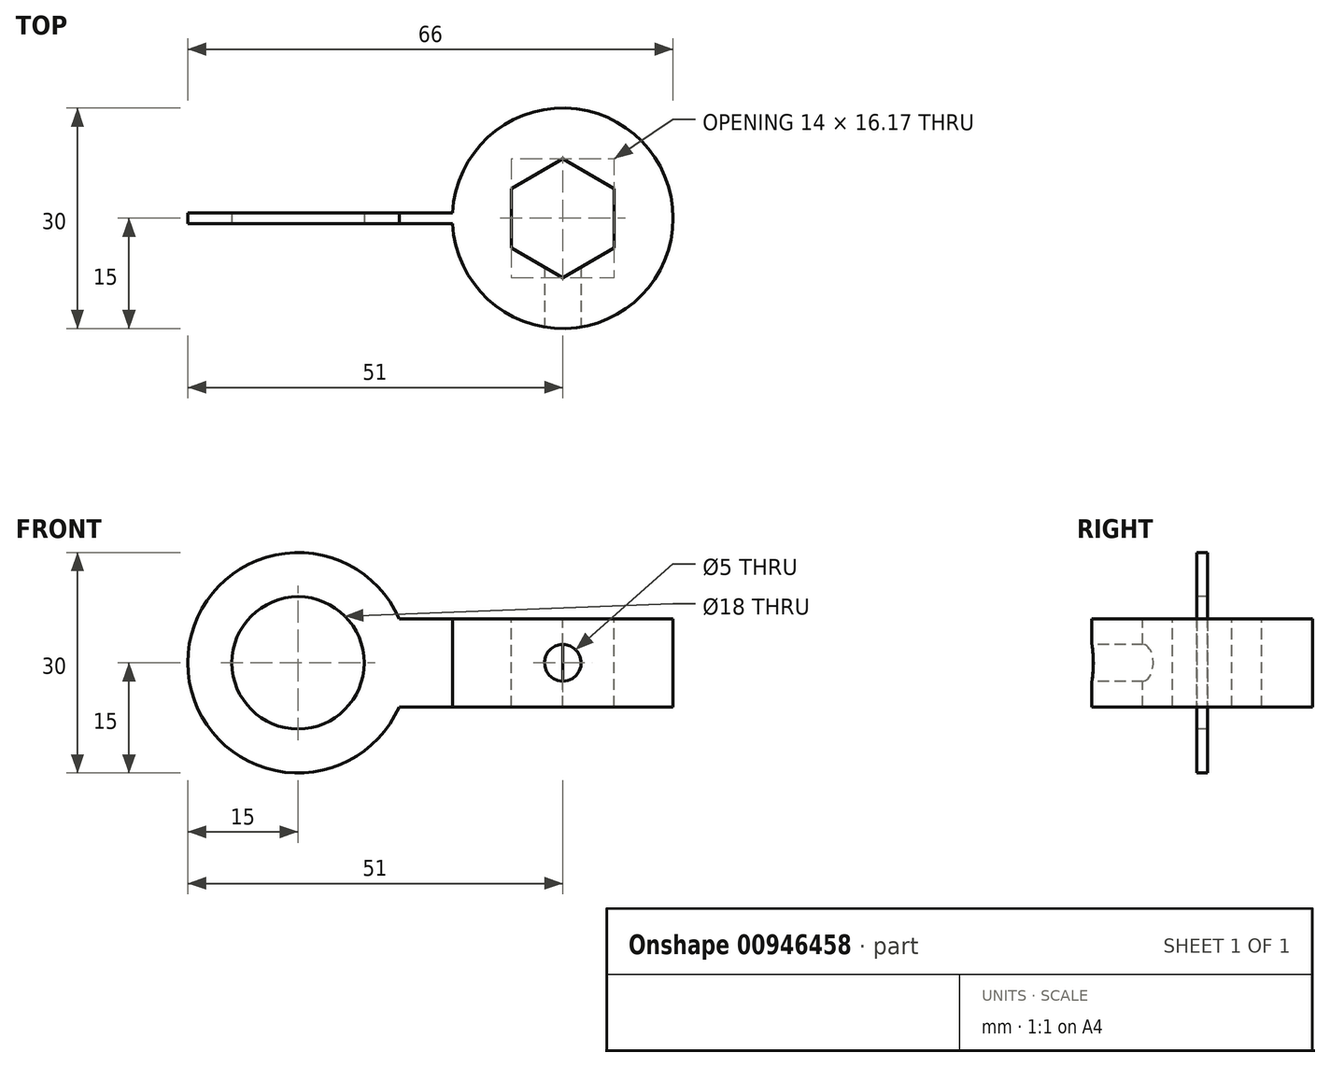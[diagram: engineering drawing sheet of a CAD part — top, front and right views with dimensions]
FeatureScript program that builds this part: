
annotation { "Feature Type Name" : "Feature", "Feature Type Description" : "" }
export const myFeature = defineFeature(function(context is Context, id is Id, definition is map)
    precondition{}
    {
        {
            var Q0;
            Q0=qCreatedBy(makeId("Top.planeOp"),FACE);
            var sketch = newSketch(context, id + "F0", { "sketchPlane" : qUnion([Q0])});
            skCircle(sketch, "E0", {"center": v(0, 0) * mm, "radius": 15 * mm});
            skSolve(sketch);
        }
        {
            var Q0;
            Q0 = qSketchRegion(id + "F0", true);
            extrude(context, id + "F1", {"entities" : qUnion([Q0]), "depth" : 12 * mm, "offsetDistance" : 25 * mm});
        }
        {
            var Q0;
            Q0=makeQuery(id+"F1.opExtrude","CAP_FACE",FACE,{"disambiguationData":[OSD([sQuery(id+"F0.wireOp",EDGE,"E0")])],"isStart":false});
            var sketch = newSketch(context, id + "F2", { "sketchPlane" : qUnion([Q0])});
            skCircle(sketch, "E1.cCircle", {"center": v(0, 0) * mm, "radius": 7 * mm, "construction": true});
            skLineSegment(sketch, "E1.0", {"start": v(7, 4.04) * mm, "end": v(7, -4.04) * mm});
            skLineSegment(sketch, "E1.1", {"start": v(7, -4.04) * mm, "end": v(0, -8.08) * mm});
            skLineSegment(sketch, "E1.2", {"start": v(0, -8.08) * mm, "end": v(-7, -4.04) * mm});
            skLineSegment(sketch, "E1.3", {"start": v(-7, -4.04) * mm, "end": v(-7, 4.04) * mm});
            skLineSegment(sketch, "E1.4", {"start": v(-7, 4.04) * mm, "end": v(0, 8.08) * mm});
            skLineSegment(sketch, "E1.5", {"start": v(0, 8.08) * mm, "end": v(7, 4.04) * mm});
            skPoint(sketch, "E1.0.midPoint", {"position": v(7, 0) * mm});
            skSolve(sketch);
        }
        {
            var Q0;
            Q0 = qSketchRegion(id + "F2", true);
            extrude(context, id + "F3", {"entities" : qUnion([Q0]), "operationType" : NewBodyOperationType.REMOVE, "endBound" : BoundingType.THROUGH_ALL, "oppositeDirection" : true, "depth" : 25 * mm, "offsetDistance" : 25 * mm});
        }
        {
            var Q0;
            Q0=qCreatedBy(makeId("Front.planeOp"),FACE);
            var sketch = newSketch(context, id + "F4", { "sketchPlane" : qUnion([Q0])});
            skLineSegment(sketch, "E2", {"start": v(0, 0) * mm, "end": v(-15, 0) * mm, "construction": true});
            skLineSegment(sketch, "E3", {"start": v(0, 0) * mm, "end": v(0, 12) * mm, "construction": true});
            skLineSegment(sketch, "E4", {"start": v(0, 12) * mm, "end": v(-15, 12) * mm, "construction": true});
            skLineSegment(sketch, "E5.bottom", {"start": v(-15, 0) * mm, "end": v(-21, 0) * mm});
            skLineSegment(sketch, "E5.top", {"start": v(-15, 12) * mm, "end": v(-21, 12) * mm});
            skLineSegment(sketch, "E5.left", {"start": v(-15, 0) * mm, "end": v(-15, 12) * mm});
            skLineSegment(sketch, "E5.right", {"start": v(-21, 0) * mm, "end": v(-21, 12) * mm});
            skPoint(sketch, "E6", {"position": v(-21, 6) * mm});
            skCircle(sketch, "E7", {"center": v(-36, 6) * mm, "radius": 15 * mm});
            skSolve(sketch);
        }
        {
            var Q0;
            Q0 = qSketchRegion(id + "F4", true);
            extrude(context, id + "F5", {"entities" : qUnion([Q0]), "endBound" : BoundingType.SYMMETRIC, "depth" : 1.5 * mm, "offsetDistance" : 25 * mm});
        }
        {
            var Q0;
            Q0=makeQuery(id+"F5.opExtrude","CAP_FACE",FACE,{"disambiguationData":[OSD([sQuery(id+"F4.wireOp",EDGE,"E7")])],"isStart":false});
            var sketch = newSketch(context, id + "F6", { "sketchPlane" : qUnion([Q0])});
            skCircle(sketch, "E8", {"center": v(-36, 6) * mm, "radius": 9 * mm});
            skSolve(sketch);
        }
        {
            var Q0;
            Q0 = qSketchRegion(id + "F6", true);
            extrude(context, id + "F7", {"entities" : qUnion([Q0]), "operationType" : NewBodyOperationType.REMOVE, "endBound" : BoundingType.THROUGH_ALL, "oppositeDirection" : true, "depth" : 25 * mm, "offsetDistance" : 25 * mm});
        }
        {
            var Q0;
            Q0=qCreatedBy(makeId("Front.planeOp"),FACE);
            cPlane(context, id + "F8", {"entities" : qUnion([Q0]), "cplaneType" : CPlaneType.OFFSET, "offset" : 15 * mm, "width" : 150 * mm, "height" : 150 * mm});
        }
        {
            var Q0;
            Q0=qCreatedBy(id+"F8.planeOp",FACE);
            var sketch = newSketch(context, id + "F9", { "sketchPlane" : qUnion([Q0])});
            skCircle(sketch, "E9", {"center": v(0, 6) * mm, "radius": 2.5 * mm});
            skSolve(sketch);
        }
        {
            var Q0;
            Q0 = qSketchRegion(id + "F9", true);
            extrude(context, id + "F10", {"entities" : qUnion([Q0]), "operationType" : NewBodyOperationType.REMOVE, "oppositeDirection" : true, "depth" : 12 * mm, "offsetDistance" : 25 * mm});
        }
        {
            var Q0;
            Q0=makeQuery(id+"F5.opExtrude","SWEPT_FACE",FACE,{"disambiguationData":[OSD([sQuery(id+"F4.wireOp",EDGE,"E5.right")])]});
            var sketch = newSketch(context, id + "F11", { "sketchPlane" : qUnion([Q0])});
            skLineSegment(sketch, "E10.0.0", {"start": v(-0.75, 12) * mm, "end": v(-0.75, 0) * mm});
            skLineSegment(sketch, "E10.0.1", {"start": v(-0.75, 0) * mm, "end": v(0.75, 0) * mm});
            skLineSegment(sketch, "E10.0.2", {"start": v(0.75, 0) * mm, "end": v(0.75, 12) * mm});
            skLineSegment(sketch, "E10.0.3", {"start": v(0.75, 12) * mm, "end": v(-0.75, 12) * mm});
            skSolve(sketch);
        }
        {
            var Q0;
            Q0=makeQuery(id+"F11.imprint","IMPRINT",FACE,{"disambiguationData":[TD([[makeQuery(id+"F11.imprint","IMPRINT",EDGE,{"derivedFrom":sQuery(id+"F11.wireOp",EDGE,"E10.0.0")}),-1.0]])]});
            var Q1;
            Q1=makeQuery(id+"F7.boolean.opBoolean","COPY",FACE,{"derivedFrom":makeQuery(id+"F7.opExtrude","SWEPT_FACE",FACE,{"disambiguationData":[OSD([sQuery(id+"F6.wireOp",EDGE,"E8")])]})});
            extrude(context, id + "F12", {"entities" : qUnion([Q0]), "operationType" : NewBodyOperationType.ADD, "endBound" : BoundingType.UP_TO_SURFACE, "depth" : 25 * mm, "endBoundEntityFace" : qUnion([Q1]), "offsetDistance" : 25 * mm});
        }
        {
            var Q0;
            Q0=makeQuery(id+"F5.opExtrude","SWEPT_FACE",FACE,{"disambiguationData":[OSD([sQuery(id+"F4.wireOp",EDGE,"E5.left")])]});
            var sketch = newSketch(context, id + "F13", { "sketchPlane" : qUnion([Q0])});
            skLineSegment(sketch, "E11.0.0", {"start": v(0.75, 0) * mm, "end": v(0.75, 12) * mm});
            skLineSegment(sketch, "E11.0.1", {"start": v(0.75, 12) * mm, "end": v(-0.75, 12) * mm});
            skLineSegment(sketch, "E11.0.2", {"start": v(-0.75, 12) * mm, "end": v(-0.75, 0) * mm});
            skLineSegment(sketch, "E11.0.3", {"start": v(-0.75, 0) * mm, "end": v(0.75, 0) * mm});
            skSolve(sketch);
        }
        {
            var Q0;
            Q0 = qSketchRegion(id + "F13", true);
            var Q1;
            Q1=makeQuery(id+"F1.opExtrude","SWEPT_FACE",FACE,{"disambiguationData":[OSD([sQuery(id+"F0.wireOp",EDGE,"E0")])]});
            extrude(context, id + "F14", {"entities" : qUnion([Q0]), "operationType" : NewBodyOperationType.ADD, "endBound" : BoundingType.UP_TO_NEXT, "depth" : 50 * mm, "endBoundEntityFace" : qUnion([Q1]), "offsetDistance" : 25 * mm});
        }
    });
